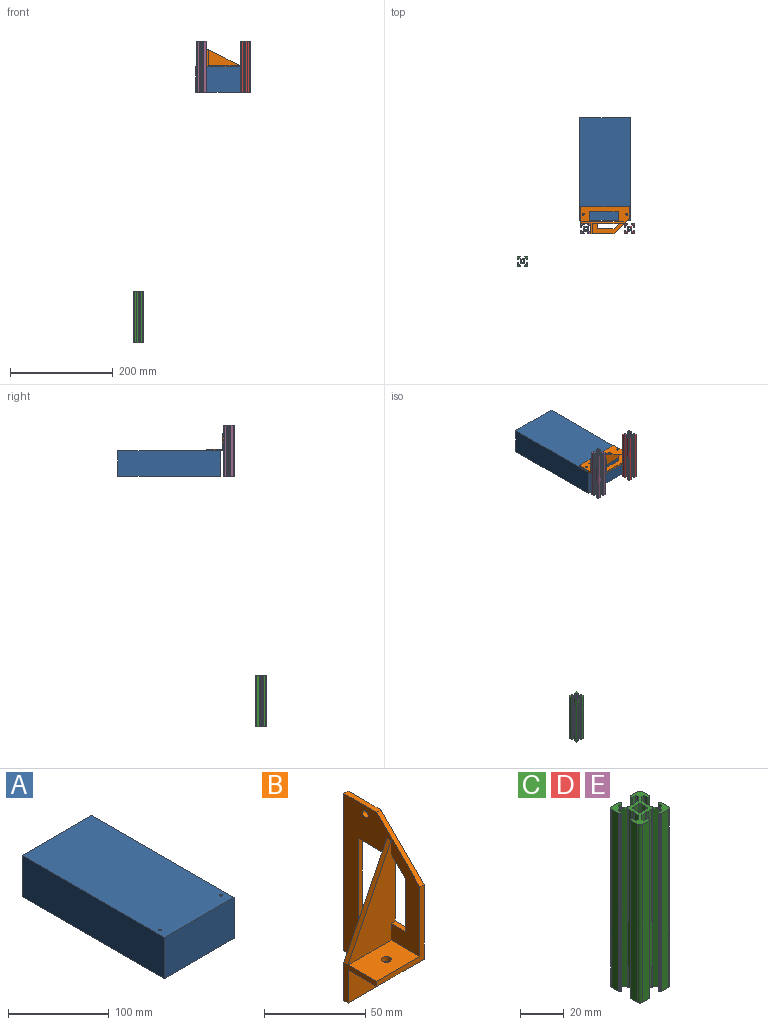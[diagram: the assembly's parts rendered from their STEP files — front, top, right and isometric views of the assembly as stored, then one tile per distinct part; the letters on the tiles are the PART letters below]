
ASSEMBLY  parts=5 mates=3
PART A: 10 faces, bbox 98x200x50 mm
  f0: plane 200x50mm, normal (1,0,0), area 10000mm2, adj f1,f3,f4,f5
  f1: plane 98x50mm, normal (0,1,0), area 4900mm2, adj f0,f2,f4,f5
  f2: plane 200x50mm, normal (-1,0,0), area 10000mm2, adj f1,f3,f4,f5
  f3: plane 98x50mm, normal (0,-1,0), area 4900mm2, adj f0,f2,f4,f5
  f4: plane 200x98mm, normal (0,0,1), area 19585.9mm2, adj f0,f1,f2,f3,f6,f8
  f5: plane 200x98mm, normal (0,0,-1), area 19600mm2, adj f0,f1,f2,f3
  f6: cylinder r=1.5mm len=25mm, axis (0,0,1), area 235.6mm2, adj f4,f7
  f7: plane 3x3mm, normal (0,0,1), area 7.1mm2, adj f6
  f8: cylinder r=1.5mm len=25mm, axis (0,0,1), area 235.6mm2, adj f4,f9
  f9: plane 3x3mm, normal (0,0,1), area 7.1mm2, adj f8
PART B: 24 faces, bbox 33x53x95 mm
  f0: plane 95x53mm, normal (-1,0,0), area 2360.9mm2, adj f2,f4,f5,f6,f7,f8,f9,f12
  f1: plane 95x53mm, normal (1,0,0), area 2669.9mm2, adj f3,f4,f5,f6,f7,f8,f9,f11
  f2: plane 30x20mm, normal (0,0,1), area 580.4mm2, adj f0,f10,f12,f14,f16
  f3: plane 33x20mm, normal (0,-1,0), area 647.4mm2, adj f1,f4,f10,f11,f15
  f4: plane 33x33mm, normal (0,0,-1), area 189mm2, adj f0,f1,f3,f5,f9,f10
  f5: plane 95x3mm, normal (0,1,0), area 285mm2, adj f0,f1,f4,f8
  f6: cylinder r=2mm len=4mm, axis (-1,0,0), area 37.7mm2, adj f0,f1
  f7: cylinder r=2mm len=4mm, axis (-1,0,0), area 37.7mm2, adj f0,f1
  f8: plane 23x3mm, normal (0,0,1), area 69mm2, adj f0,f1,f5,f13
  f9: plane 83x33mm, normal (0,1,0), area 1745.4mm2, adj f0,f1,f4,f10,f15,f17,f22,f23
  f10: plane 23x23mm, normal (-1,0,0), area 129mm2, adj f2,f3,f4,f9,f11,f12,f17
  f11: plane 33x20mm, normal (0,0,-1), area 640.4mm2, adj f1,f3,f10,f12,f14
  f12: plane 45x33mm, normal (0,-1,0), area 225mm2, adj f0,f1,f2,f10,f11,f13
  f13: plane 30x30mm, normal (0,-0.71,0.71), area 127.3mm2, adj f0,f1,f8,f12
  f14: cylinder r=2.5mm len=5mm, axis (0,0,-1), area 47.1mm2, adj f2,f11
  f15: cylinder r=2mm len=4mm, axis (0,-1,0), area 37.7mm2, adj f3,f9
  f16: plane 60x33mm, normal (0,-1,0), area 1026mm2, adj f0,f1,f2,f17,f19,f20
  f17: plane 60x30mm, normal (-0.89,0,0.45), area 201.2mm2, adj f0,f9,f10,f16
  f18: plane 32x3mm, normal (0,1,0), area 96mm2, adj f0,f1,f19,f20
  f19: plane 10x3mm, normal (0,0,1), area 30mm2, adj f0,f1,f16,f18
  f20: plane 10x10mm, normal (0,0.71,-0.71), area 42.4mm2, adj f0,f1,f16,f18
  f21: plane 56x3mm, normal (0,-1,0), area 168mm2, adj f0,f1,f22,f23
  f22: plane 20x3mm, normal (0,0,1), area 60mm2, adj f0,f1,f9,f21
  f23: plane 20x3mm, normal (0,0,-1), area 60mm2, adj f0,f1,f9,f21
PART C: 154 faces, bbox 20x20x100 mm
  f0: cylinder r=3.55mm len=100mm, axis (0,0,1), area 153.8mm2, adj f1,f151,f152,f153
  f1: plane 100x0.65mm, normal (0.77,0.64,0), area 85.1mm2, adj f0,f2,f152,f153
  f2: cylinder r=2.75mm len=100mm, axis (0,0,1), area 261.4mm2, adj f1,f3,f152,f153
  f3: plane 100x0.65mm, normal (0.77,-0.64,0), area 85.1mm2, adj f2,f4,f152,f153
  f4: cylinder r=3.55mm len=100mm, axis (0,0,1), area 153.8mm2, adj f3,f5,f152,f153
  f5: plane 100x0.66mm, normal (-0.64,0.77,0), area 85.2mm2, adj f4,f6,f152,f153
  f6: cylinder r=2.75mm len=100mm, axis (0,0,1), area 261.4mm2, adj f5,f7,f152,f153
  f7: plane 100x0.66mm, normal (0.64,0.77,0), area 85.2mm2, adj f6,f8,f152,f153
  f8: cylinder r=3.55mm len=100mm, axis (0,0,1), area 153.8mm2, adj f7,f9,f152,f153
  f9: plane 100x0.65mm, normal (-0.77,-0.64,0), area 85.1mm2, adj f8,f10,f152,f153
  f10: cylinder r=2.75mm len=100mm, axis (0,0,1), area 261.4mm2, adj f9,f11,f152,f153
  f11: plane 100x0.65mm, normal (-0.77,0.64,0), area 85.1mm2, adj f10,f12,f152,f153
  f12: cylinder r=3.55mm len=100mm, axis (0,0,1), area 153.8mm2, adj f11,f13,f152,f153
  f13: plane 100x0.66mm, normal (0.64,-0.77,0), area 85.2mm2, adj f12,f14,f152,f153
  f14: cylinder r=2.75mm len=100mm, axis (0,0,1), area 261.4mm2, adj f13,f151,f152,f153
  f15: cylinder r=1.5mm len=100mm, axis (0,0,1), area 235.6mm2, adj f16,f150,f152,f153
  f16: plane 100x4.65mm, normal (0,1,0), area 465mm2, adj f15,f17,f152,f153
  f17: cylinder r=0.2mm len=100mm, axis (0,0,1), area 31.4mm2, adj f16,f18,f152,f153
  f18: plane 100x0.3mm, normal (1,0,0), area 30mm2, adj f17,f19,f152,f153
  f19: plane 100x0.35mm, normal (0,1,0), area 35mm2, adj f18,f20,f152,f153
  f20: cylinder r=0.2mm len=100mm, axis (0,0,1), area 31.4mm2, adj f19,f21,f152,f153
  f21: plane 100x0.3mm, normal (1,0,0), area 30mm2, adj f20,f22,f152,f153
  f22: cylinder r=0.5mm len=100mm, axis (0,0,1), area 78.5mm2, adj f21,f23,f152,f153
  f23: plane 100x1.9mm, normal (0,-1,0), area 190mm2, adj f22,f24,f152,f153
  f24: cylinder r=0.5mm len=100mm, axis (0,0,1), area 78.5mm2, adj f23,f25,f152,f153
  f25: plane 100x0.73mm, normal (1,0,0), area 73.2mm2, adj f24,f26,f152,f153
  f26: cylinder r=0.5mm len=100mm, axis (0,0,1), area 39.3mm2, adj f25,f27,f152,f153
  f27: plane 100x2.27mm, normal (0.71,0.71,0), area 320.7mm2, adj f26,f28,f152,f153
  f28: cylinder r=0.5mm len=100mm, axis (0,0,1), area 39.3mm2, adj f27,f29,f152,f153
  f29: plane 100x2.28mm, normal (0,1,0), area 227.9mm2, adj f28,f30,f152,f153
  f30: cylinder r=0.2mm len=100mm, axis (0,0,1), area 10.5mm2, adj f29,f31,f152,f153
  f31: plane 100x0.75mm, normal (0.5,0.87,0), area 87mm2, adj f30,f32,f152,f153
  f32: cylinder r=0.2mm len=100mm, axis (0,0,1), area 20.9mm2, adj f31,f33,f152,f153
  f33: plane 100x0.75mm, normal (-0.5,0.87,0), area 87mm2, adj f32,f34,f152,f153
  f34: cylinder r=0.2mm len=100mm, axis (0,0,1), area 10.5mm2, adj f33,f35,f152,f153
  f35: plane 100x2.28mm, normal (0,1,0), area 227.9mm2, adj f34,f36,f152,f153
  f36: cylinder r=0.5mm len=100mm, axis (0,0,1), area 39.3mm2, adj f35,f37,f152,f153
  f37: plane 100x2.27mm, normal (-0.71,0.71,0), area 320.7mm2, adj f36,f38,f152,f153
  f38: cylinder r=0.5mm len=100mm, axis (0,0,1), area 39.3mm2, adj f37,f39,f152,f153
  f39: plane 100x0.73mm, normal (-1,0,0), area 73.2mm2, adj f38,f40,f152,f153
  f40: cylinder r=0.5mm len=100mm, axis (0,0,1), area 78.5mm2, adj f39,f41,f152,f153
  f41: plane 100x1.9mm, normal (0,-1,0), area 190mm2, adj f40,f42,f152,f153
  f42: cylinder r=0.5mm len=100mm, axis (0,0,1), area 78.5mm2, adj f41,f43,f152,f153
  f43: plane 100x0.3mm, normal (-1,0,0), area 30mm2, adj f42,f44,f152,f153
  f44: cylinder r=0.2mm len=100mm, axis (0,0,1), area 31.4mm2, adj f43,f45,f152,f153
  f45: plane 100x0.35mm, normal (0,1,0), area 35mm2, adj f44,f46,f152,f153
  f46: plane 100x0.3mm, normal (-1,0,0), area 30mm2, adj f45,f47,f152,f153
  f47: cylinder r=0.2mm len=100mm, axis (0,0,1), area 31.4mm2, adj f46,f48,f152,f153
  f48: plane 100x4.65mm, normal (0,1,0), area 465mm2, adj f47,f49,f152,f153
  f49: cylinder r=1.5mm len=100mm, axis (0,0,1), area 235.6mm2, adj f48,f50,f152,f153
  f50: plane 100x4.65mm, normal (1,0,0), area 465mm2, adj f49,f51,f152,f153
  f51: cylinder r=0.2mm len=100mm, axis (0,0,1), area 31.4mm2, adj f50,f52,f152,f153
  f52: plane 100x0.3mm, normal (0,-1,0), area 30mm2, adj f51,f53,f152,f153
  f53: plane 100x0.35mm, normal (1,0,0), area 35mm2, adj f52,f54,f152,f153
  f54: cylinder r=0.2mm len=100mm, axis (0,0,1), area 31.4mm2, adj f53,f55,f152,f153
  f55: plane 100x0.3mm, normal (0,-1,0), area 30mm2, adj f54,f56,f152,f153
  f56: cylinder r=0.5mm len=100mm, axis (0,0,1), area 78.5mm2, adj f55,f57,f152,f153
  f57: plane 100x1.9mm, normal (-1,0,0), area 190mm2, adj f56,f58,f152,f153
  f58: cylinder r=0.5mm len=100mm, axis (0,0,1), area 78.5mm2, adj f57,f59,f152,f153
  f59: plane 100x0.73mm, normal (0,-1,0), area 73.2mm2, adj f58,f60,f152,f153
  f60: cylinder r=0.5mm len=100mm, axis (0,0,1), area 39.3mm2, adj f59,f61,f152,f153
  f61: plane 100x2.27mm, normal (0.71,-0.71,0), area 320.7mm2, adj f60,f62,f152,f153
  f62: cylinder r=0.5mm len=100mm, axis (0,0,1), area 39.3mm2, adj f61,f63,f152,f153
  f63: plane 100x2.28mm, normal (1,0,0), area 227.9mm2, adj f62,f64,f152,f153
  f64: cylinder r=0.2mm len=100mm, axis (0,0,1), area 10.5mm2, adj f63,f65,f152,f153
  f65: plane 100x0.75mm, normal (0.87,-0.5,0), area 87mm2, adj f64,f66,f152,f153
  f66: cylinder r=0.2mm len=100mm, axis (0,0,1), area 20.9mm2, adj f65,f67,f152,f153
  f67: plane 100x0.75mm, normal (0.87,0.5,0), area 87mm2, adj f66,f68,f152,f153
  f68: cylinder r=0.2mm len=100mm, axis (0,0,1), area 10.5mm2, adj f67,f69,f152,f153
  f69: plane 100x2.28mm, normal (1,0,0), area 227.9mm2, adj f68,f70,f152,f153
  f70: cylinder r=0.5mm len=100mm, axis (0,0,1), area 39.3mm2, adj f69,f71,f152,f153
  f71: plane 100x2.27mm, normal (0.71,0.71,0), area 320.7mm2, adj f70,f72,f152,f153
  f72: cylinder r=0.5mm len=100mm, axis (0,0,1), area 39.3mm2, adj f71,f73,f152,f153
  f73: plane 100x0.73mm, normal (0,1,0), area 73.2mm2, adj f72,f74,f152,f153
  f74: cylinder r=0.5mm len=100mm, axis (0,0,1), area 78.5mm2, adj f73,f75,f152,f153
  f75: plane 100x1.9mm, normal (-1,0,0), area 190mm2, adj f74,f76,f152,f153
  f76: cylinder r=0.5mm len=100mm, axis (0,0,1), area 78.5mm2, adj f75,f77,f152,f153
  f77: plane 100x0.3mm, normal (0,1,0), area 30mm2, adj f76,f78,f152,f153
  f78: cylinder r=0.2mm len=100mm, axis (0,0,1), area 31.4mm2, adj f77,f79,f152,f153
  f79: plane 100x0.35mm, normal (1,0,0), area 35mm2, adj f78,f80,f152,f153
  f80: plane 100x0.3mm, normal (0,1,0), area 30mm2, adj f79,f81,f152,f153
  f81: cylinder r=0.2mm len=100mm, axis (0,0,1), area 31.4mm2, adj f80,f82,f152,f153
  f82: plane 100x4.65mm, normal (1,0,0), area 465mm2, adj f81,f83,f152,f153
  f83: cylinder r=1.5mm len=100mm, axis (0,0,1), area 235.6mm2, adj f82,f84,f152,f153
  f84: plane 100x4.65mm, normal (0,-1,0), area 465mm2, adj f83,f85,f152,f153
  f85: cylinder r=0.2mm len=100mm, axis (0,0,1), area 31.4mm2, adj f84,f86,f152,f153
  f86: plane 100x0.3mm, normal (-1,0,0), area 30mm2, adj f85,f87,f152,f153
  f87: plane 100x0.35mm, normal (0,-1,0), area 35mm2, adj f86,f88,f152,f153
  f88: cylinder r=0.2mm len=100mm, axis (0,0,1), area 31.4mm2, adj f87,f89,f152,f153
  f89: plane 100x0.3mm, normal (-1,0,0), area 30mm2, adj f88,f90,f152,f153
  f90: cylinder r=0.5mm len=100mm, axis (0,0,1), area 78.5mm2, adj f89,f91,f152,f153
  f91: plane 100x1.9mm, normal (0,1,0), area 190mm2, adj f90,f92,f152,f153
  f92: cylinder r=0.5mm len=100mm, axis (0,0,1), area 78.5mm2, adj f91,f93,f152,f153
  f93: plane 100x0.73mm, normal (-1,0,0), area 73.2mm2, adj f92,f94,f152,f153
  f94: cylinder r=0.5mm len=100mm, axis (0,0,1), area 39.3mm2, adj f93,f95,f152,f153
  f95: plane 100x2.27mm, normal (-0.71,-0.71,0), area 320.7mm2, adj f94,f96,f152,f153
  f96: cylinder r=0.5mm len=100mm, axis (0,0,1), area 39.3mm2, adj f95,f97,f152,f153
  f97: plane 100x2.28mm, normal (0,-1,0), area 227.9mm2, adj f96,f98,f152,f153
  f98: cylinder r=0.2mm len=100mm, axis (0,0,1), area 10.5mm2, adj f97,f99,f152,f153
  f99: plane 100x0.75mm, normal (-0.5,-0.87,0), area 87mm2, adj f98,f100,f152,f153
  f100: cylinder r=0.2mm len=100mm, axis (0,0,1), area 20.9mm2, adj f99,f101,f152,f153
  f101: plane 100x0.75mm, normal (0.5,-0.87,0), area 87mm2, adj f100,f102,f152,f153
  f102: cylinder r=0.2mm len=100mm, axis (0,0,1), area 10.5mm2, adj f101,f103,f152,f153
  f103: plane 100x2.28mm, normal (0,-1,0), area 227.9mm2, adj f102,f104,f152,f153
  f104: cylinder r=0.5mm len=100mm, axis (0,0,1), area 39.3mm2, adj f103,f105,f152,f153
  f105: plane 100x2.27mm, normal (0.71,-0.71,0), area 320.7mm2, adj f104,f106,f152,f153
  f106: cylinder r=0.5mm len=100mm, axis (0,0,1), area 39.3mm2, adj f105,f107,f152,f153
  f107: plane 100x0.73mm, normal (1,0,0), area 73.2mm2, adj f106,f108,f152,f153
  f108: cylinder r=0.5mm len=100mm, axis (0,0,1), area 78.5mm2, adj f107,f109,f152,f153
  f109: plane 100x1.9mm, normal (0,1,0), area 190mm2, adj f108,f110,f152,f153
  f110: cylinder r=0.5mm len=100mm, axis (0,0,1), area 78.5mm2, adj f109,f111,f152,f153
  f111: plane 100x0.3mm, normal (1,0,0), area 30mm2, adj f110,f112,f152,f153
  f112: cylinder r=0.2mm len=100mm, axis (0,0,1), area 31.4mm2, adj f111,f113,f152,f153
  f113: plane 100x0.35mm, normal (0,-1,0), area 35mm2, adj f112,f114,f152,f153
  f114: plane 100x0.3mm, normal (1,0,0), area 30mm2, adj f113,f115,f152,f153
  f115: cylinder r=0.2mm len=100mm, axis (0,0,1), area 31.4mm2, adj f114,f116,f152,f153
  f116: plane 100x4.65mm, normal (0,-1,0), area 465mm2, adj f115,f117,f152,f153
  f117: cylinder r=1.5mm len=100mm, axis (0,0,1), area 235.6mm2, adj f116,f118,f152,f153
  f118: plane 100x4.65mm, normal (-1,0,0), area 465mm2, adj f117,f119,f152,f153
  f119: cylinder r=0.2mm len=100mm, axis (0,0,1), area 31.4mm2, adj f118,f120,f152,f153
  f120: plane 100x0.3mm, normal (0,1,0), area 30mm2, adj f119,f121,f152,f153
  f121: plane 100x0.35mm, normal (-1,0,0), area 35mm2, adj f120,f122,f152,f153
  f122: cylinder r=0.2mm len=100mm, axis (0,0,1), area 31.4mm2, adj f121,f123,f152,f153
  f123: plane 100x0.3mm, normal (0,1,0), area 30mm2, adj f122,f124,f152,f153
  f124: cylinder r=0.5mm len=100mm, axis (0,0,1), area 78.5mm2, adj f123,f125,f152,f153
  f125: plane 100x1.9mm, normal (1,0,0), area 190mm2, adj f124,f126,f152,f153
  f126: cylinder r=0.5mm len=100mm, axis (0,0,1), area 78.5mm2, adj f125,f127,f152,f153
  f127: plane 100x0.73mm, normal (0,1,0), area 73.2mm2, adj f126,f128,f152,f153
  f128: cylinder r=0.5mm len=100mm, axis (0,0,1), area 39.3mm2, adj f127,f129,f152,f153
  f129: plane 100x2.27mm, normal (-0.71,0.71,0), area 320.7mm2, adj f128,f130,f152,f153
  f130: cylinder r=0.5mm len=100mm, axis (0,0,1), area 39.3mm2, adj f129,f131,f152,f153
  f131: plane 100x2.28mm, normal (-1,0,0), area 227.9mm2, adj f130,f132,f152,f153
  f132: cylinder r=0.2mm len=100mm, axis (0,0,1), area 10.5mm2, adj f131,f133,f152,f153
  f133: plane 100x0.75mm, normal (-0.87,0.5,0), area 87mm2, adj f132,f134,f152,f153
  f134: cylinder r=0.2mm len=100mm, axis (0,0,1), area 20.9mm2, adj f133,f135,f152,f153
  f135: plane 100x0.75mm, normal (-0.87,-0.5,0), area 87mm2, adj f134,f136,f152,f153
  f136: cylinder r=0.2mm len=100mm, axis (0,0,1), area 10.5mm2, adj f135,f137,f152,f153
  f137: plane 100x2.28mm, normal (-1,0,0), area 227.9mm2, adj f136,f138,f152,f153
  f138: cylinder r=0.5mm len=100mm, axis (0,0,1), area 39.3mm2, adj f137,f139,f152,f153
  f139: plane 100x2.27mm, normal (-0.71,-0.71,0), area 320.7mm2, adj f138,f140,f152,f153
  f140: cylinder r=0.5mm len=100mm, axis (0,0,1), area 39.3mm2, adj f139,f141,f152,f153
  f141: plane 100x0.73mm, normal (0,-1,0), area 73.2mm2, adj f140,f142,f152,f153
  f142: cylinder r=0.5mm len=100mm, axis (0,0,1), area 78.5mm2, adj f141,f143,f152,f153
  f143: plane 100x1.9mm, normal (1,0,0), area 190mm2, adj f142,f144,f152,f153
  f144: cylinder r=0.5mm len=100mm, axis (0,0,1), area 78.5mm2, adj f143,f145,f152,f153
  f145: plane 100x0.3mm, normal (0,-1,0), area 30mm2, adj f144,f146,f152,f153
  f146: cylinder r=0.2mm len=100mm, axis (0,0,1), area 31.4mm2, adj f145,f147,f152,f153
  f147: plane 100x0.35mm, normal (-1,0,0), area 35mm2, adj f146,f148,f152,f153
  f148: plane 100x0.3mm, normal (0,-1,0), area 30mm2, adj f147,f149,f152,f153
  f149: cylinder r=0.2mm len=100mm, axis (0,0,1), area 31.4mm2, adj f148,f150,f152,f153
  f150: plane 100x4.65mm, normal (-1,0,0), area 465mm2, adj f15,f149,f152,f153
  f151: plane 100x0.66mm, normal (-0.64,-0.77,0), area 85.2mm2, adj f0,f14,f152,f153
  f152: plane 20x20mm, normal (0,0,-1), area 162mm2, adj f0,f1,f2,f3,f4,f5,f6,f7
  f153: plane 20x20mm, normal (0,0,1), area 162mm2, adj f0,f1,f2,f3,f4,f5,f6,f7
PART D: same geometry as C
PART E: same geometry as C
PLACE A rot(axis=(1,0,0),0deg) t=(-156.38,-4.95,-63.52)mm
PLACE B rot(axis=(0,1,0),90deg) t=(-156.38,-92.95,-10.52)mm
PLACE C t=(-325.29,-193.44,-450.81)mm
PLACE D t=(-117.38,-130.95,36.48)mm
PLACE E t=(-202.38,-130.95,36.48)mm
MATE planar B.f11 <-> E.f50  axis (-1,0,0) through (-183.88,-110.95,-13.52)mm
MATE fastened A.f8 <-> B.f6  axis (0,0,1) through (-113.88,-92.95,-13.52)mm
MATE fastened D.f153 <-> E.f153  axis (0,0,1) through (-118.88,-127.13,36.48)mm
